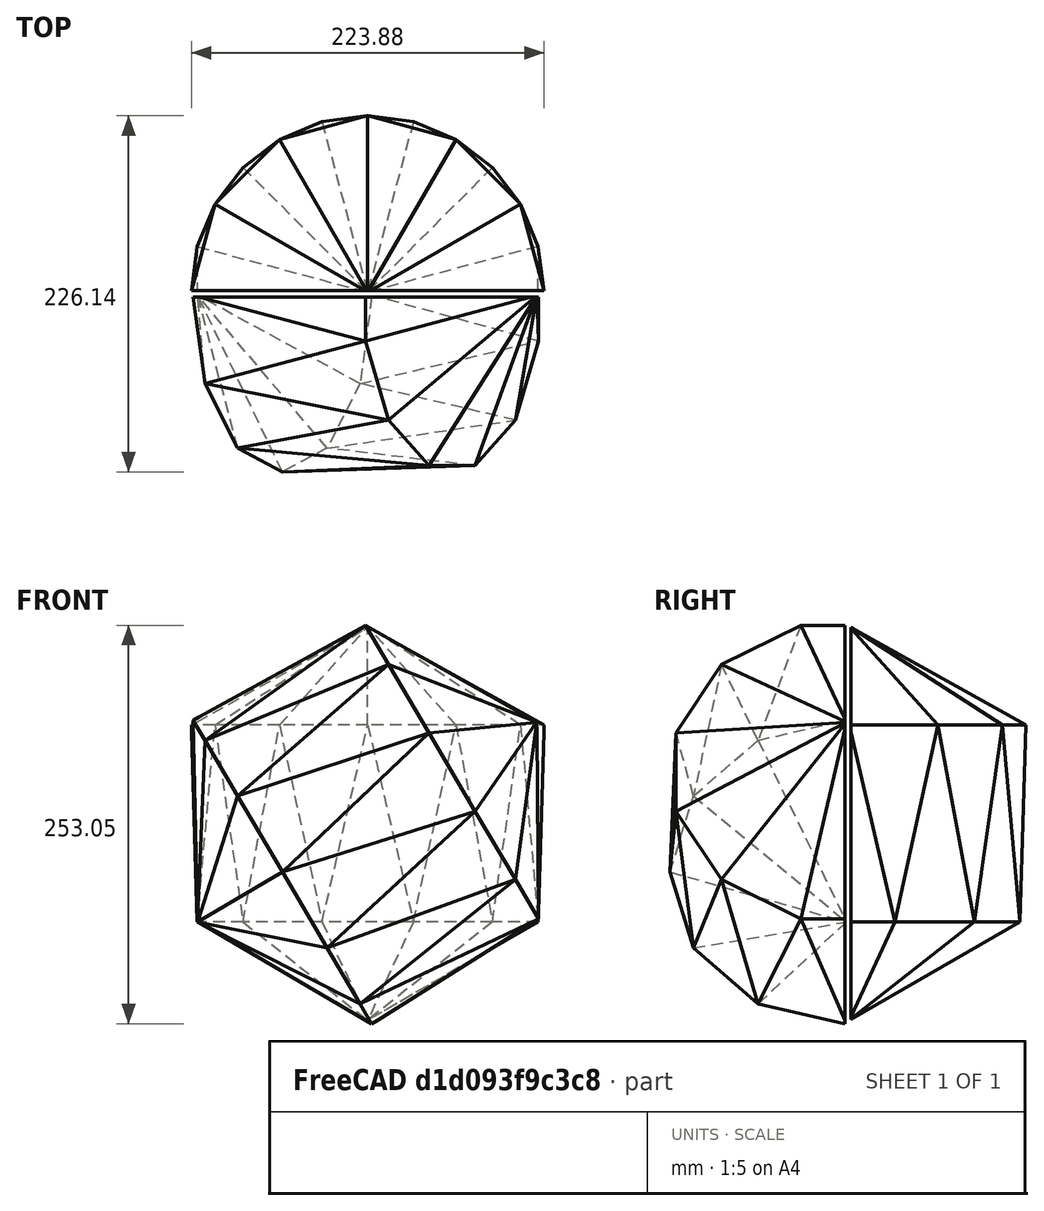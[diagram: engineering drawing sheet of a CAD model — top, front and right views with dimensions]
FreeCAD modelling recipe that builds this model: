
FCSTD DOCUMENT  (FreeCAD 0.18R16110 (Git))
Label: streptohedron
License: All rights reserved
LicenseURL: http://en.wikipedia.org/wiki/All_rights_reserved
objects: Part::Feature×2, Part::Box×2, Part::MultiCommon×2
note: 6 computed .brp shape members not serialized (recipe doc carries the construction recipe); baked Part::Feature solids carry a one-line shape summary decoded from their .brp

FEATURE [Part::Feature] Shape
  shape: bbox 224.1 x 224.1 x 250 mm, 48 faces (baked)
FEATURE [Part::Box] Box  label="Kubus"
  AttacherType = Attacher::AttachEngine3D
  Height = 500
  Length = 500
  Placement = pos=(-232,1,-176) rot=(0,0,1;0rad)
  Width = 500
FEATURE [Part::MultiCommon] Common
  Shapes = -> [Shape,Box]
FEATURE [Part::Box] Box001  label="Kubus001"
  AttacherType = Attacher::AttachEngine3D
  Height = 500
  Length = 500
  Placement = pos=(-232,1,-176) rot=(0,0,1;0rad)
  Width = 500
FEATURE [Part::Feature] Shape001
  shape: bbox 224.1 x 224.1 x 250 mm, 48 faces (baked)
FEATURE [Part::MultiCommon] Common001
  Placement = pos=(-0.317025,-2,0.883218) rot=(0.868199,0,-0.496217;3.14159rad)
  Shapes = -> [Shape001,Box001]
